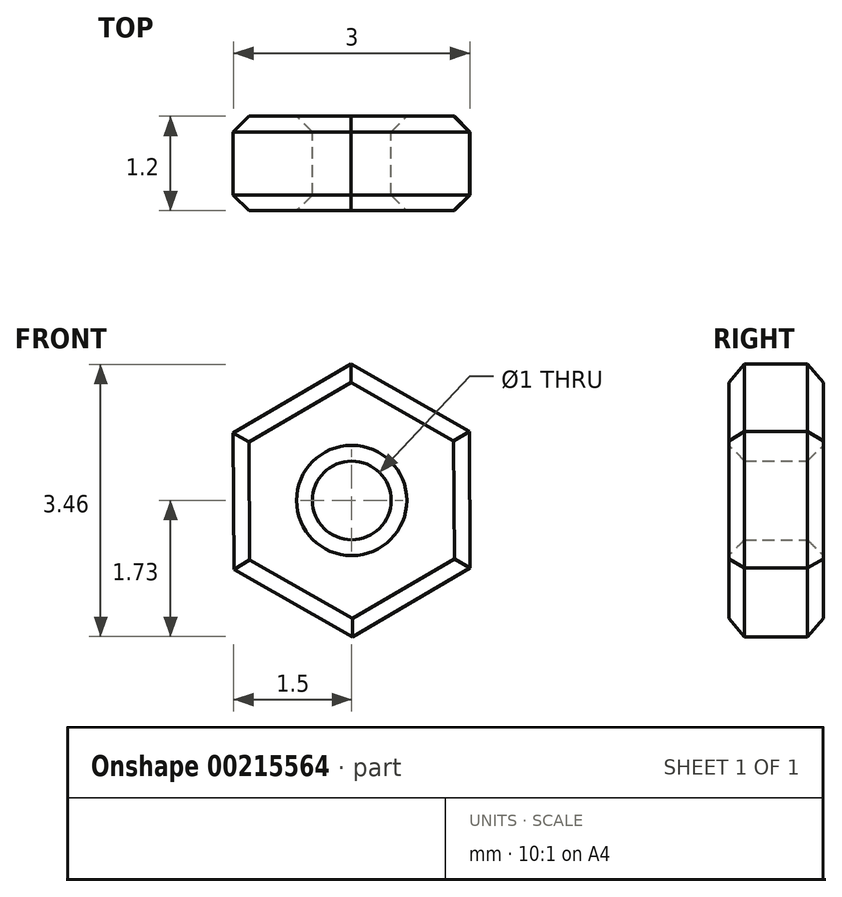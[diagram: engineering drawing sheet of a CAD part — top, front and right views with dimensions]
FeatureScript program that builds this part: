
annotation { "Feature Type Name" : "Feature", "Feature Type Description" : "" }
export const myFeature = defineFeature(function(context is Context, id is Id, definition is map)
    precondition{}
    {
        {
            var Q0;
            Q0=qCreatedBy(makeId("Front.planeOp"),FACE);
            var sketch = newSketch(context, id + "F0", { "sketchPlane" : qUnion([Q0])});
            skCircle(sketch, "E0", {"center": v(0, 0) * mm, "radius": 0.5 * mm});
            skPoint(sketch, "E1.0.midPoint", {"position": v(0.53, -0.93) * mm});
            skCircle(sketch, "E2.cCircle", {"center": v(0, 0) * mm, "radius": 1.5 * mm, "construction": true});
            skLineSegment(sketch, "E2.0", {"start": v(1.5, -0.86) * mm, "end": v(0, -1.73) * mm});
            skLineSegment(sketch, "E2.1", {"start": v(0, -1.73) * mm, "end": v(-1.5, -0.87) * mm});
            skLineSegment(sketch, "E2.2", {"start": v(-1.5, -0.87) * mm, "end": v(-1.5, 0.86) * mm});
            skLineSegment(sketch, "E2.3", {"start": v(-1.5, 0.86) * mm, "end": v(0, 1.73) * mm});
            skLineSegment(sketch, "E2.4", {"start": v(0, 1.73) * mm, "end": v(1.5, 0.87) * mm});
            skLineSegment(sketch, "E2.5", {"start": v(1.5, 0.87) * mm, "end": v(1.5, -0.86) * mm});
            skPoint(sketch, "E2.0.midPoint", {"position": v(0.76, -1.3) * mm});
            skSolve(sketch);
        }
        {
            var Q0;
            Q0 = qSketchRegion(id + "F0", true);
            extrude(context, id + "F1", {"entities" : qUnion([Q0]), "depth" : 1.2 * mm});
        }
        {
            var Q0;
            Q0=makeQuery(id+"F1.opExtrude","CAP_FACE",FACE,{"disambiguationData":[OSD([sQuery(id+"F0.wireOp",EDGE,"E0"),sQuery(id+"F0.wireOp",EDGE,"E2.0"),sQuery(id+"F0.wireOp",EDGE,"E2.1"),sQuery(id+"F0.wireOp",EDGE,"E2.2"),sQuery(id+"F0.wireOp",EDGE,"E2.3"),sQuery(id+"F0.wireOp",EDGE,"E2.4"),sQuery(id+"F0.wireOp",EDGE,"E2.5")])],"isStart":true});
            var Q1;
            Q1=makeQuery(id+"F1.opExtrude","CAP_FACE",FACE,{"disambiguationData":[OSD([sQuery(id+"F0.wireOp",EDGE,"E0"),sQuery(id+"F0.wireOp",EDGE,"E2.0"),sQuery(id+"F0.wireOp",EDGE,"E2.1"),sQuery(id+"F0.wireOp",EDGE,"E2.2"),sQuery(id+"F0.wireOp",EDGE,"E2.3"),sQuery(id+"F0.wireOp",EDGE,"E2.4"),sQuery(id+"F0.wireOp",EDGE,"E2.5")])],"isStart":false});
            chamfer(context, id + "F2", {"entities" : qUnion([Q0, Q1]), "width" : 0.2 * mm, "tangentPropagation" : true});
        }
    });
